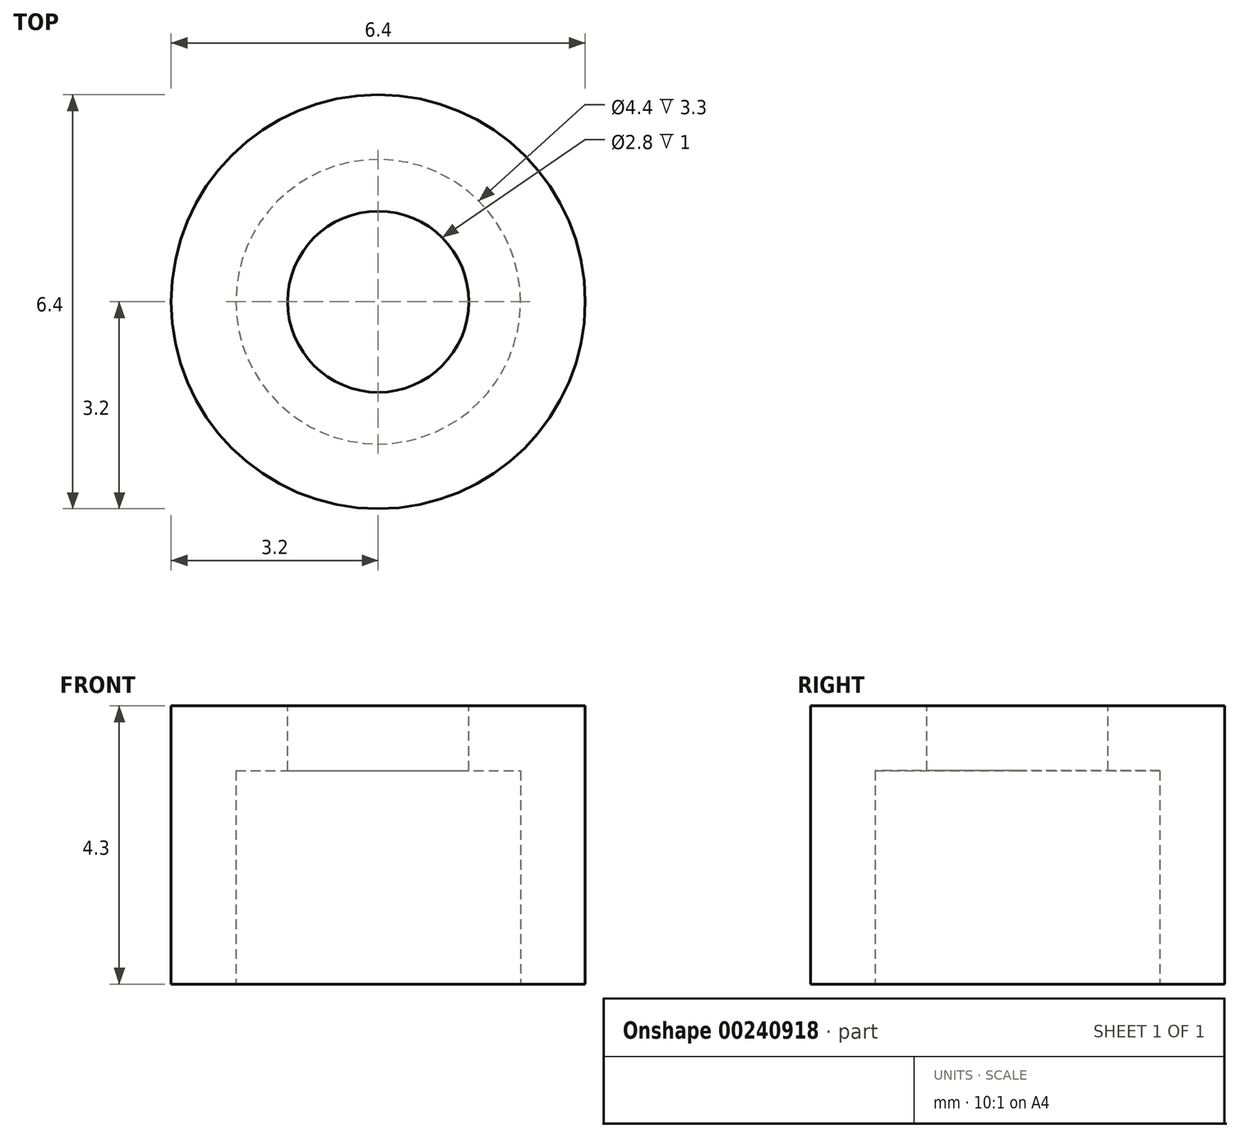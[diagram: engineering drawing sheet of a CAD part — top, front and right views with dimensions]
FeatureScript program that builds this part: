
annotation { "Feature Type Name" : "Feature", "Feature Type Description" : "" }
export const myFeature = defineFeature(function(context is Context, id is Id, definition is map)
    precondition{}
    {
        {
            var Q0;
            Q0=qCreatedBy(makeId("Top.planeOp"),FACE);
            var sketch = newSketch(context, id + "F0", { "sketchPlane" : qUnion([Q0])});
            skCircle(sketch, "E0", {"center": v(0, 0) * mm, "radius": 3.2 * mm});
            skSolve(sketch);
        }
        {
            var Q0;
            Q0=makeQuery(id+"F0.imprint","IMPRINT",FACE,{"disambiguationData":[TD([[makeQuery(id+"F0.imprint","IMPRINT",EDGE,{"derivedFrom":sQuery(id+"F0.wireOp",EDGE,"E0")}),1.0]])]});
            extrude(context, id + "F1", {"entities" : qUnion([Q0]), "depth" : 4.3 * mm});
        }
        {
            var Q0;
            Q0=makeQuery(id+"F1.opExtrude","CAP_FACE",FACE,{"disambiguationData":[OSD([sQuery(id+"F0.wireOp",EDGE,"E0")])],"isStart":true});
            var sketch = newSketch(context, id + "F2", { "sketchPlane" : qUnion([Q0])});
            skCircle(sketch, "E1", {"center": v(0, 0) * mm, "radius": 2.2 * mm});
            skSolve(sketch);
        }
        {
            var Q0;
            Q0 = qSketchRegion(id + "F2", true);
            extrude(context, id + "F3", {"entities" : qUnion([Q0]), "operationType" : NewBodyOperationType.REMOVE, "oppositeDirection" : true, "depth" : 3.3 * mm});
        }
        {
            var Q0;
            Q0=makeQuery(id+"F1.opExtrude","CAP_FACE",FACE,{"disambiguationData":[OSD([sQuery(id+"F0.wireOp",EDGE,"E0")])],"isStart":false});
            var sketch = newSketch(context, id + "F4", { "sketchPlane" : qUnion([Q0])});
            skCircle(sketch, "E2", {"center": v(0, 0) * mm, "radius": 1.4 * mm});
            skSolve(sketch);
        }
        {
            var Q0;
            Q0 = qSketchRegion(id + "F4", true);
            extrude(context, id + "F5", {"entities" : qUnion([Q0]), "operationType" : NewBodyOperationType.REMOVE, "oppositeDirection" : true, "depth" : 25 * mm});
        }
    });
